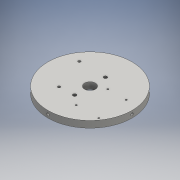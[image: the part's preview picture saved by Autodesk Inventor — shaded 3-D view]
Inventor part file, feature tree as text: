
AUTODESK INVENTOR PART (.ipt)
format: ipt  version: 2016 (Build 200138000, 138)  size: 180,224 bytes
history: native  units: mm
features: extrude x8, sketch x7, thread x6, other x5
ambient origin geometry x8: Origin, YZ Plane, XZ Plane, XY Plane, X Axis, Y Axis, Z Axis, Center Point
bodies: Body1 (feature_tree)
feature tree (26):
  other  "ソリッド1"
  extrude  "押し出し1"  Depth=101.0mm
  other  "作業平面1"
  other  "作業平面2"
  other  "作業平面3"
  other  "作業平面4"
  extrude  "押し出し2"  Depth=8.0mm TaperAngle=0.0deg
  extrude  "押し出し3"  Depth=50.5mm
  extrude  "押し出し4"  Depth=4.0mm
  extrude  "押し出し5"  Depth=3.0mm
  thread  "ねじ1"
  thread  "ねじ2"
  thread  "ねじ3"
  thread  "ねじ4"
  extrude  "押し出し7"  Depth=5.0mm TaperAngle=0.0deg
  thread  "ねじ7"
  thread  "ねじ8"
  sketch  "スケッチ9"
  extrude  "押し出し10"  Depth=4.0mm
  extrude  "押し出し11"  Depth=3.0mm
  sketch  "スケッチ1"
  sketch  "スケッチ2"
  sketch  "スケッチ3"
  sketch  "スケッチ4"
  sketch  "スケッチ5"
  sketch  "スケッチ10"
